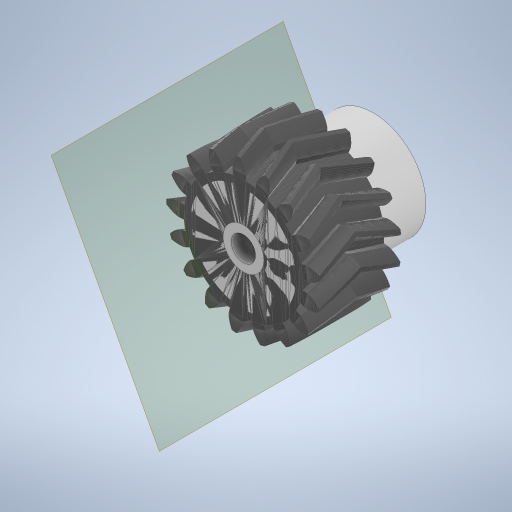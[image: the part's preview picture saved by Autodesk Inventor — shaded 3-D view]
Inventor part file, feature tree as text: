
AUTODESK INVENTOR PART (.ipt)
format: ipt  version: 2024.2 (Build 282272000, 272)  size: 570,368 bytes
history: native  units: in
note: dims shown in document units (in); Inventor stores cm internally (conversion verified against a paired STEP export)
features: other x2, extrude x2, sketch x2, plane x1
ambient origin geometry x8: Origin, YZ Plane, XZ Plane, XY Plane, X Axis, Y Axis, Z Axis, Center Point
bodies: Solid1 (feature_tree)
feature tree (7):
  other  "gears_5mm_17T"
  extrude  "Extrusion1"  Depth=0.1181in
  plane  "Work Plane1"
  extrude  "Extrusion2"  Depth=0.0787in
  sketch  "Sketch1"  dims[d0=0.5118in d1=0.1181in]
  sketch  "Sketch2"  dims[d2=0.2362in d3=0.3937in d4=0.0in d5=0.0in d6=0.1575in d7=0.0787in d8=0.315in d9=0.0in]
  other  "MeshFeature1"
